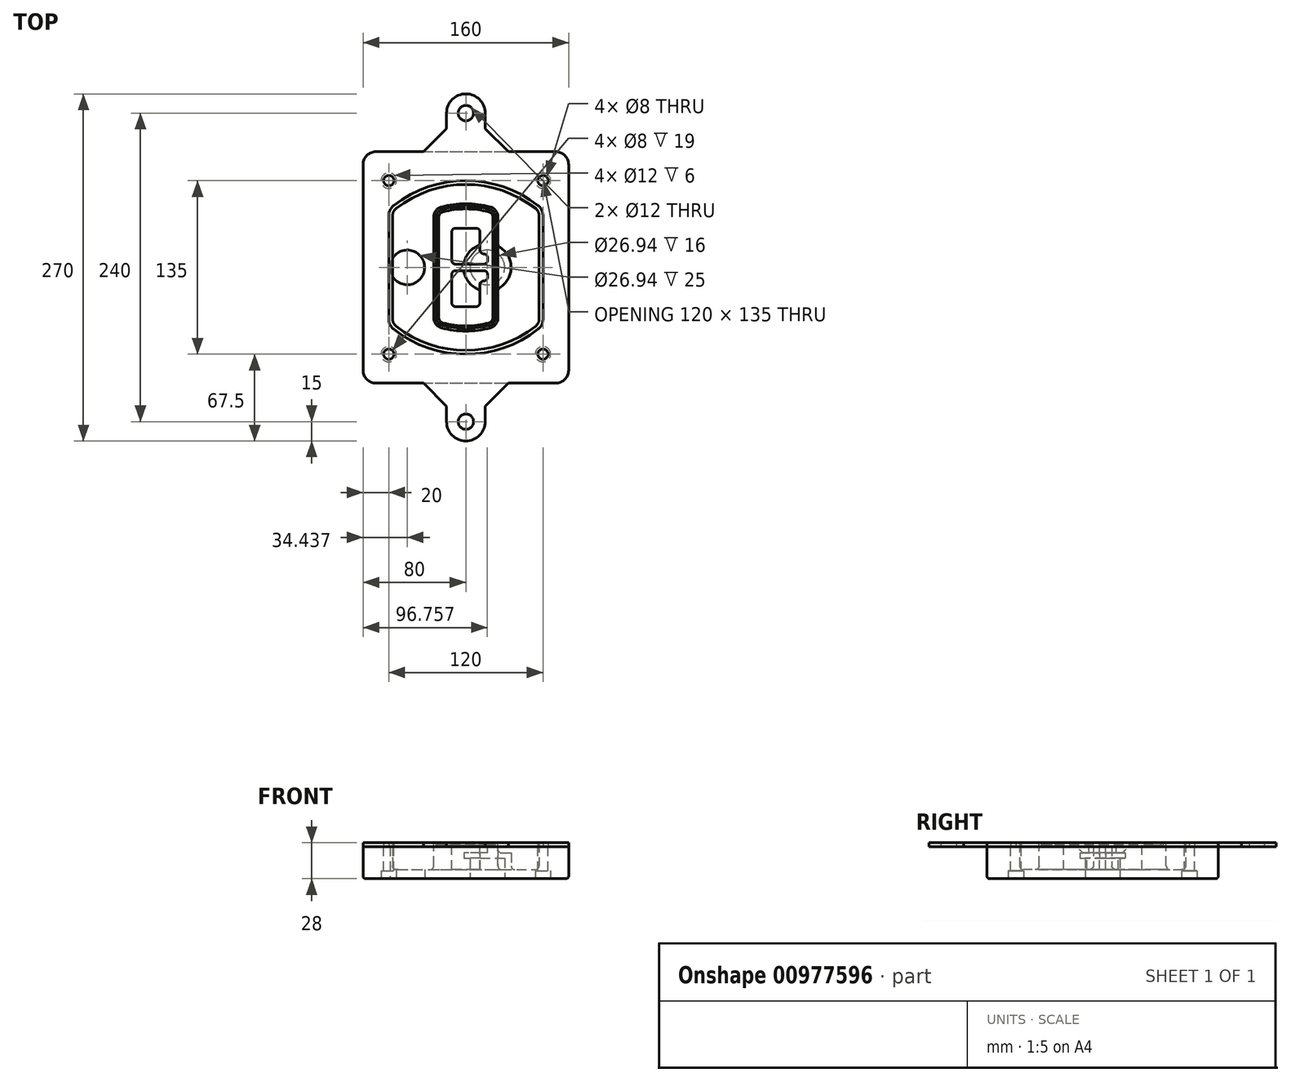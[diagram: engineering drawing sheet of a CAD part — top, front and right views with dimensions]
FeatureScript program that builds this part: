
annotation { "Feature Type Name" : "Feature", "Feature Type Description" : "" }
export const myFeature = defineFeature(function(context is Context, id is Id, definition is map)
    precondition{}
    {
        {
            var Q0;
            Q0=qCreatedBy(makeId("Top.planeOp"),FACE);
            var sketch = newSketch(context, id + "F0", { "sketchPlane" : qUnion([Q0])});
            skPoint(sketch, "E0.rect.middle", {"position": v(0, 0) * mm});
            skLineSegment(sketch, "E1.bottom", {"start": v(-70, -90) * mm, "end": v(70, -90) * mm});
            skLineSegment(sketch, "E1.top", {"start": v(-70, 90) * mm, "end": v(70, 90) * mm});
            skLineSegment(sketch, "E1.left", {"start": v(-80, -80) * mm, "end": v(-80, 80) * mm});
            skLineSegment(sketch, "E1.right", {"start": v(80, -80) * mm, "end": v(80, 80) * mm});
            skLineSegment(sketch, "E2", {"start": v(-80, 90) * mm, "end": v(80, -90) * mm, "construction": true});
            skLineSegment(sketch, "E3", {"start": v(80, 90) * mm, "end": v(-80, -90) * mm, "construction": true});
            skCircle(sketch, "E4", {"center": v(-60, 67.5) * mm, "radius": 4 * mm});
            skCircle(sketch, "E5", {"center": v(60, 67.5) * mm, "radius": 4 * mm});
            skCircle(sketch, "E6", {"center": v(60, -67.5) * mm, "radius": 4 * mm});
            skCircle(sketch, "E7", {"center": v(-60, -67.5) * mm, "radius": 4 * mm});
            skLineSegment(sketch, "E8", {"start": v(-60, 67.5) * mm, "end": v(60, 67.5) * mm, "construction": true});
            skLineSegment(sketch, "E9", {"start": v(60, 67.5) * mm, "end": v(60, -67.5) * mm, "construction": true});
            skLineSegment(sketch, "E10", {"start": v(60, -67.5) * mm, "end": v(-60, -67.5) * mm, "construction": true});
            skLineSegment(sketch, "E11", {"start": v(-60, -67.5) * mm, "end": v(-60, 67.5) * mm, "construction": true});
            skLineSegment(sketch, "E12", {"start": v(-60, 40.3) * mm, "end": v(-60, -40.3) * mm});
            skLineSegment(sketch, "E13", {"start": v(60, 40.3) * mm, "end": v(60, -40.3) * mm});
            skArc(sketch, "E14", {"start": v(56.15, 48.18) * mm, "mid": v(0, 67.5) * mm, "end": v(-56.15, 48.18) * mm});
            skArc(sketch, "E15", {"start": v(-56.15, -48.18) * mm, "mid": v(0, -67.5) * mm, "end": v(56.15, -48.18) * mm});
            skLineSegment(sketch, "E16", {"start": v(-60, 0) * mm, "end": v(60, 0) * mm, "construction": true});
            skPoint(sketch, "E17.visualSharp", {"position": v(-60, -45) * mm});
            skArc(sketch, "E17.filletArc", {"start": v(-60, -40.3) * mm, "mid": v(-58.99, -44.68) * mm, "end": v(-56.15, -48.18) * mm});
            skPoint(sketch, "E18.visualSharp", {"position": v(-60, 45) * mm});
            skArc(sketch, "E18.filletArc", {"start": v(-56.15, 48.18) * mm, "mid": v(-58.99, 44.68) * mm, "end": v(-60, 40.3) * mm});
            skPoint(sketch, "E19.visualSharp", {"position": v(60, 45) * mm});
            skArc(sketch, "E19.filletArc", {"start": v(60, 40.3) * mm, "mid": v(58.99, 44.68) * mm, "end": v(56.15, 48.18) * mm});
            skPoint(sketch, "E20.visualSharp", {"position": v(60, -45) * mm});
            skArc(sketch, "E20.filletArc", {"start": v(56.15, -48.18) * mm, "mid": v(58.99, -44.68) * mm, "end": v(60, -40.3) * mm});
            skPoint(sketch, "E21.visualSharp", {"position": v(-80, 90) * mm});
            skArc(sketch, "E21.filletArc", {"start": v(-70, 90) * mm, "mid": v(-77.07, 87.07) * mm, "end": v(-80, 80) * mm});
            skPoint(sketch, "E22.visualSharp", {"position": v(80, 90) * mm});
            skArc(sketch, "E22.filletArc", {"start": v(80, 80) * mm, "mid": v(77.07, 87.07) * mm, "end": v(70, 90) * mm});
            skPoint(sketch, "E23.visualSharp", {"position": v(80, -90) * mm});
            skArc(sketch, "E23.filletArc", {"start": v(70, -90) * mm, "mid": v(77.07, -87.07) * mm, "end": v(80, -80) * mm});
            skPoint(sketch, "E24.visualSharp", {"position": v(-80, -90) * mm});
            skArc(sketch, "E24.filletArc", {"start": v(-80, -80) * mm, "mid": v(-77.07, -87.07) * mm, "end": v(-70, -90) * mm});
            skArc(sketch, "E25.0", {"start": v(57, 40.3) * mm, "mid": v(56.3, 43.36) * mm, "end": v(54.3, 45.81) * mm});
            skLineSegment(sketch, "E25.1", {"start": v(57, 40.3) * mm, "end": v(57, -40.3) * mm});
            skArc(sketch, "E25.2", {"start": v(54.3, -45.81) * mm, "mid": v(56.3, -43.36) * mm, "end": v(57, -40.3) * mm});
            skArc(sketch, "E25.3", {"start": v(-54.3, -45.81) * mm, "mid": v(0, -64.5) * mm, "end": v(54.3, -45.81) * mm});
            skArc(sketch, "E25.4", {"start": v(-57, -40.3) * mm, "mid": v(-56.3, -43.36) * mm, "end": v(-54.3, -45.81) * mm});
            skArc(sketch, "E25.5", {"start": v(54.3, 45.81) * mm, "mid": v(0, 64.5) * mm, "end": v(-54.3, 45.81) * mm});
            skLineSegment(sketch, "E25.6", {"start": v(-57, 40.3) * mm, "end": v(-57, -40.3) * mm});
            skArc(sketch, "E25.7", {"start": v(-54.3, 45.81) * mm, "mid": v(-56.3, 43.36) * mm, "end": v(-57, 40.3) * mm});
            skArc(sketch, "E26.0", {"start": v(-58.62, 51.33) * mm, "mid": v(-62.58, 46.43) * mm, "end": v(-64, 40.3) * mm});
            skArc(sketch, "E26.1", {"start": v(58.62, 51.33) * mm, "mid": v(0, 71.5) * mm, "end": v(-58.62, 51.33) * mm});
            skArc(sketch, "E26.2", {"start": v(64, 40.3) * mm, "mid": v(62.58, 46.43) * mm, "end": v(58.62, 51.33) * mm});
            skLineSegment(sketch, "E26.3", {"start": v(64, 40.3) * mm, "end": v(64, -40.3) * mm});
            skArc(sketch, "E26.4", {"start": v(58.62, -51.33) * mm, "mid": v(62.58, -46.43) * mm, "end": v(64, -40.3) * mm});
            skLineSegment(sketch, "E26.5", {"start": v(-64, 40.3) * mm, "end": v(-64, -40.3) * mm});
            skArc(sketch, "E26.6", {"start": v(-58.62, -51.33) * mm, "mid": v(0, -71.5) * mm, "end": v(58.62, -51.33) * mm});
            skArc(sketch, "E26.7", {"start": v(-64, -40.3) * mm, "mid": v(-62.58, -46.43) * mm, "end": v(-58.62, -51.33) * mm});
            skSolve(sketch);
        }
        {
            var Q0;
            Q0=makeQuery(id+"F0.imprint","IMPRINT",FACE,{"disambiguationData":[TD([[makeQuery(id+"F0.imprint","IMPRINT",EDGE,{"derivedFrom":sQuery(id+"F0.wireOp",EDGE,"E1.bottom")}),1.0]])]});
            var Q1;
            Q1=makeQuery(id+"F0.imprint","IMPRINT",FACE,{"disambiguationData":[TD([[makeQuery(id+"F0.imprint","IMPRINT",EDGE,{"derivedFrom":sQuery(id+"F0.wireOp",EDGE,"E12")}),1.0]])]});
            var Q2;
            Q2=makeQuery(id+"F0.imprint","IMPRINT",FACE,{"disambiguationData":[TD([[makeQuery(id+"F0.imprint","IMPRINT",EDGE,{"derivedFrom":sQuery(id+"F0.wireOp",EDGE,"E25.0")}),1.0]])]});
            var Q3;
            Q3=makeQuery(id+"F0.imprint","IMPRINT",FACE,{"disambiguationData":[TD([[makeQuery(id+"F0.imprint","IMPRINT",EDGE,{"derivedFrom":sQuery(id+"F0.wireOp",EDGE,"E12")}),-1.0]])]});
            extrude(context, id + "F1", {"entities" : qUnion([Q0, Q1, Q2, Q3]), "oppositeDirection" : true, "depth" : 25 * mm});
        }
        {
            var Q0;
            Q0=makeQuery(id+"F0.imprint","IMPRINT",FACE,{"disambiguationData":[TD([[makeQuery(id+"F0.imprint","IMPRINT",EDGE,{"derivedFrom":sQuery(id+"F0.wireOp",EDGE,"E12")}),1.0]])]});
            extrude(context, id + "F2", {"entities" : qUnion([Q0]), "operationType" : NewBodyOperationType.ADD, "depth" : 3 * mm});
        }
        {
            var Q0;
            Q0=makeQuery(id+"F0.imprint","IMPRINT",FACE,{"disambiguationData":[TD([[makeQuery(id+"F0.imprint","IMPRINT",EDGE,{"derivedFrom":sQuery(id+"F0.wireOp",EDGE,"E25.0")}),1.0]])]});
            extrude(context, id + "F3", {"entities" : qUnion([Q0]), "operationType" : NewBodyOperationType.REMOVE, "oppositeDirection" : true, "depth" : 18 * mm});
        }
        {
            var Q0;
            Q0=makeQuery(id+"F2.opExtrude","CAP_FACE",FACE,{"disambiguationData":[OSD([sQuery(id+"F0.wireOp",EDGE,"E12"),sQuery(id+"F0.wireOp",EDGE,"E13"),sQuery(id+"F0.wireOp",EDGE,"E14"),sQuery(id+"F0.wireOp",EDGE,"E15"),sQuery(id+"F0.wireOp",EDGE,"E17.filletArc"),sQuery(id+"F0.wireOp",EDGE,"E18.filletArc"),sQuery(id+"F0.wireOp",EDGE,"E19.filletArc"),sQuery(id+"F0.wireOp",EDGE,"E20.filletArc"),sQuery(id+"F0.wireOp",EDGE,"E25.0"),sQuery(id+"F0.wireOp",EDGE,"E25.1"),sQuery(id+"F0.wireOp",EDGE,"E25.2"),sQuery(id+"F0.wireOp",EDGE,"E25.3"),sQuery(id+"F0.wireOp",EDGE,"E25.4"),sQuery(id+"F0.wireOp",EDGE,"E25.5"),sQuery(id+"F0.wireOp",EDGE,"E25.6"),sQuery(id+"F0.wireOp",EDGE,"E25.7")])],"isStart":false});
            var sketch = newSketch(context, id + "F4", { "sketchPlane" : qUnion([Q0])});
            skArc(sketch, "E27.0", {"start": v(-19.08, -46.97) * mm, "mid": v(0, -49.5) * mm, "end": v(19.08, -46.97) * mm});
            skArc(sketch, "E28.0", {"start": v(19.08, 46.97) * mm, "mid": v(0, 49.5) * mm, "end": v(-19.08, 46.97) * mm});
            skLineSegment(sketch, "E29", {"start": v(-25, 39.25) * mm, "end": v(-25, -39.25) * mm});
            skLineSegment(sketch, "E30", {"start": v(25, 39.25) * mm, "end": v(25, -39.25) * mm});
            skLineSegment(sketch, "E31", {"start": v(-25, 45.1) * mm, "end": v(25, 45.1) * mm, "construction": true});
            skLineSegment(sketch, "E32", {"start": v(-25, -45.1) * mm, "end": v(25, -45.1) * mm, "construction": true});
            skPoint(sketch, "E33.visualSharp", {"position": v(-25, 45.1) * mm});
            skArc(sketch, "E33.filletArc", {"start": v(-19.08, 46.97) * mm, "mid": v(-23.35, 44.11) * mm, "end": v(-25, 39.25) * mm});
            skPoint(sketch, "E34.visualSharp", {"position": v(25, 45.1) * mm});
            skArc(sketch, "E34.filletArc", {"start": v(25, 39.25) * mm, "mid": v(23.35, 44.11) * mm, "end": v(19.08, 46.97) * mm});
            skPoint(sketch, "E35.visualSharp", {"position": v(25, -45.1) * mm});
            skArc(sketch, "E35.filletArc", {"start": v(19.08, -46.97) * mm, "mid": v(23.35, -44.11) * mm, "end": v(25, -39.25) * mm});
            skPoint(sketch, "E36.visualSharp", {"position": v(-25, -45.1) * mm});
            skArc(sketch, "E36.filletArc", {"start": v(-25, -39.25) * mm, "mid": v(-23.35, -44.11) * mm, "end": v(-19.08, -46.97) * mm});
            skArc(sketch, "E37.0", {"start": v(54.3, 45.81) * mm, "mid": v(0, 64.5) * mm, "end": v(-54.3, 45.81) * mm});
            skArc(sketch, "E37.1", {"start": v(-54.3, 45.81) * mm, "mid": v(-56.3, 43.36) * mm, "end": v(-57, 40.3) * mm});
            skLineSegment(sketch, "E37.2", {"start": v(-57, 40.3) * mm, "end": v(-57, -40.3) * mm});
            skArc(sketch, "E37.3", {"start": v(-57, -40.3) * mm, "mid": v(-56.3, -43.36) * mm, "end": v(-54.3, -45.81) * mm});
            skArc(sketch, "E37.4", {"start": v(-54.3, -45.81) * mm, "mid": v(0, -64.5) * mm, "end": v(54.3, -45.81) * mm});
            skArc(sketch, "E37.5", {"start": v(54.3, -45.81) * mm, "mid": v(56.3, -43.36) * mm, "end": v(57, -40.3) * mm});
            skLineSegment(sketch, "E37.6", {"start": v(57, 40.3) * mm, "end": v(57, -40.3) * mm});
            skArc(sketch, "E37.7", {"start": v(57, 40.3) * mm, "mid": v(56.3, 43.36) * mm, "end": v(54.3, 45.81) * mm});
            skLineSegment(sketch, "E38.0", {"start": v(23, 39.25) * mm, "end": v(23, -39.25) * mm});
            skArc(sketch, "E38.1", {"start": v(18.56, -45.04) * mm, "mid": v(21.76, -42.9) * mm, "end": v(23, -39.25) * mm});
            skArc(sketch, "E38.2", {"start": v(-18.56, -45.04) * mm, "mid": v(0, -47.5) * mm, "end": v(18.56, -45.04) * mm});
            skArc(sketch, "E38.3", {"start": v(-23, -39.25) * mm, "mid": v(-21.76, -42.9) * mm, "end": v(-18.56, -45.04) * mm});
            skLineSegment(sketch, "E38.4", {"start": v(-23, 39.25) * mm, "end": v(-23, -39.25) * mm});
            skArc(sketch, "E38.5", {"start": v(23, 39.25) * mm, "mid": v(21.76, 42.9) * mm, "end": v(18.56, 45.04) * mm});
            skArc(sketch, "E38.6", {"start": v(-18.56, 45.04) * mm, "mid": v(-21.76, 42.9) * mm, "end": v(-23, 39.25) * mm});
            skArc(sketch, "E38.7", {"start": v(18.56, 45.04) * mm, "mid": v(0, 47.5) * mm, "end": v(-18.56, 45.04) * mm});
            skArc(sketch, "E39.0", {"start": v(21, 39.25) * mm, "mid": v(20.18, 41.68) * mm, "end": v(18.04, 43.1) * mm});
            skLineSegment(sketch, "E39.1", {"start": v(21, 39.25) * mm, "end": v(21, -39.25) * mm});
            skArc(sketch, "E39.2", {"start": v(18.04, -43.1) * mm, "mid": v(20.18, -41.68) * mm, "end": v(21, -39.25) * mm});
            skArc(sketch, "E39.3", {"start": v(-18.04, -43.1) * mm, "mid": v(0, -45.5) * mm, "end": v(18.04, -43.1) * mm});
            skArc(sketch, "E39.4", {"start": v(-21, -39.25) * mm, "mid": v(-20.18, -41.68) * mm, "end": v(-18.04, -43.1) * mm});
            skArc(sketch, "E39.5", {"start": v(18.04, 43.1) * mm, "mid": v(0, 45.5) * mm, "end": v(-18.04, 43.1) * mm});
            skLineSegment(sketch, "E39.6", {"start": v(-21, 39.25) * mm, "end": v(-21, -39.25) * mm});
            skArc(sketch, "E39.7", {"start": v(-18.04, 43.1) * mm, "mid": v(-20.18, 41.68) * mm, "end": v(-21, 39.25) * mm});
            skLineSegment(sketch, "E40", {"start": v(-25, 0) * mm, "end": v(25, 0) * mm, "construction": true});
            skLineSegment(sketch, "E41", {"start": v(-11, 5.5) * mm, "end": v(-11, 27.5) * mm});
            skLineSegment(sketch, "E42", {"start": v(-8, 30.5) * mm, "end": v(8, 30.5) * mm});
            skLineSegment(sketch, "E43", {"start": v(11, 27.5) * mm, "end": v(11, 13.5) * mm});
            skLineSegment(sketch, "E44", {"start": v(14, 10.5) * mm, "end": v(14, 10.5) * mm});
            skLineSegment(sketch, "E45", {"start": v(17, 7.5) * mm, "end": v(17, 5.5) * mm});
            skLineSegment(sketch, "E46", {"start": v(14, 2.5) * mm, "end": v(-8, 2.5) * mm});
            skPoint(sketch, "E47.visualSharp", {"position": v(-11, 30.5) * mm});
            skArc(sketch, "E47.filletArc", {"start": v(-8, 30.5) * mm, "mid": v(-10.12, 29.62) * mm, "end": v(-11, 27.5) * mm});
            skPoint(sketch, "E48.visualSharp", {"position": v(11, 30.5) * mm});
            skArc(sketch, "E48.filletArc", {"start": v(11, 27.5) * mm, "mid": v(10.12, 29.62) * mm, "end": v(8, 30.5) * mm});
            skPoint(sketch, "E49.visualSharp", {"position": v(11, 10.5) * mm});
            skArc(sketch, "E49.filletArc", {"start": v(11, 13.5) * mm, "mid": v(11.88, 11.38) * mm, "end": v(14, 10.5) * mm});
            skPoint(sketch, "E50.visualSharp", {"position": v(17, 10.5) * mm});
            skArc(sketch, "E50.filletArc", {"start": v(17, 7.5) * mm, "mid": v(16.12, 9.62) * mm, "end": v(14, 10.5) * mm});
            skPoint(sketch, "E51.visualSharp", {"position": v(17, 2.5) * mm});
            skArc(sketch, "E51.filletArc", {"start": v(14, 2.5) * mm, "mid": v(16.12, 3.38) * mm, "end": v(17, 5.5) * mm});
            skPoint(sketch, "E52.visualSharp", {"position": v(-11, 2.5) * mm});
            skArc(sketch, "E52.filletArc", {"start": v(-11, 5.5) * mm, "mid": v(-10.12, 3.38) * mm, "end": v(-8, 2.5) * mm});
            skLineSegment(sketch, "E53.0.MirrorCS", {"start": v(14, -2.5) * mm, "end": v(-8, -2.5) * mm});
            skArc(sketch, "E54.0.MirrorCS", {"start": v(-11, -5.5) * mm, "mid": v(-10.12, -3.38) * mm, "end": v(-8, -2.5) * mm});
            skLineSegment(sketch, "E55.0.MirrorCS", {"start": v(-11, -5.5) * mm, "end": v(-11, -27.5) * mm});
            skArc(sketch, "E56.0.MirrorCS", {"start": v(-8, -30.5) * mm, "mid": v(-10.12, -29.62) * mm, "end": v(-11, -27.5) * mm});
            skLineSegment(sketch, "E57.0.MirrorCS", {"start": v(-8, -30.5) * mm, "end": v(8, -30.5) * mm});
            skArc(sketch, "E58.0.MirrorCS", {"start": v(11, -27.5) * mm, "mid": v(10.12, -29.62) * mm, "end": v(8, -30.5) * mm});
            skLineSegment(sketch, "E59.0.MirrorCS", {"start": v(11, -27.5) * mm, "end": v(11, -13.5) * mm});
            skArc(sketch, "E60.0.MirrorCS", {"start": v(11, -13.5) * mm, "mid": v(11.88, -11.38) * mm, "end": v(14, -10.5) * mm});
            skArc(sketch, "E61.0.MirrorCS", {"start": v(17, -7.5) * mm, "mid": v(16.12, -9.62) * mm, "end": v(14, -10.5) * mm});
            skLineSegment(sketch, "E62.0.MirrorCS", {"start": v(17, -7.5) * mm, "end": v(17, -5.5) * mm});
            skArc(sketch, "E63.0.MirrorCS", {"start": v(14, -2.5) * mm, "mid": v(16.12, -3.38) * mm, "end": v(17, -5.5) * mm});
            skSolve(sketch);
        }
        {
            var Q0;
            Q0=makeQuery(id+"F4.imprint","IMPRINT",FACE,{"disambiguationData":[TD([[makeQuery(id+"F4.imprint","IMPRINT",EDGE,{"derivedFrom":sQuery(id+"F4.wireOp",EDGE,"E27.0")}),1.0]])]});
            var Q1;
            Q1=makeQuery(id+"F4.imprint","IMPRINT",FACE,{"disambiguationData":[TD([[makeQuery(id+"F4.imprint","IMPRINT",EDGE,{"derivedFrom":sQuery(id+"F4.wireOp",EDGE,"E38.0")}),-1.0]])]});
            var Q2;
            Q2=makeQuery(id+"F4.imprint","IMPRINT",FACE,{"disambiguationData":[TD([[makeQuery(id+"F4.imprint","IMPRINT",EDGE,{"derivedFrom":sQuery(id+"F4.wireOp",EDGE,"E39.0")}),1.0]])]});
            extrude(context, id + "F5", {"entities" : qUnion([Q0, Q1, Q2]), "operationType" : NewBodyOperationType.ADD, "endBound" : BoundingType.UP_TO_NEXT, "oppositeDirection" : true, "depth" : 25 * mm});
        }
        {
            var Q0;
            Q0=makeQuery(id+"F4.imprint","IMPRINT",FACE,{"disambiguationData":[TD([[makeQuery(id+"F4.imprint","IMPRINT",EDGE,{"derivedFrom":sQuery(id+"F4.wireOp",EDGE,"E38.0")}),-1.0]])]});
            extrude(context, id + "F6", {"entities" : qUnion([Q0]), "operationType" : NewBodyOperationType.REMOVE, "oppositeDirection" : true, "depth" : 2 * mm});
        }
        {
            var Q0;
            Q0=makeQuery(id+"F1.opExtrude","CAP_FACE",FACE,{"disambiguationData":[OSD([sQuery(id+"F0.wireOp",EDGE,"E1.bottom"),sQuery(id+"F0.wireOp",EDGE,"E1.top"),sQuery(id+"F0.wireOp",EDGE,"E1.left"),sQuery(id+"F0.wireOp",EDGE,"E1.right"),sQuery(id+"F0.wireOp",EDGE,"E4"),sQuery(id+"F0.wireOp",EDGE,"E5"),sQuery(id+"F0.wireOp",EDGE,"E6"),sQuery(id+"F0.wireOp",EDGE,"E7"),sQuery(id+"F0.wireOp",EDGE,"E21.filletArc"),sQuery(id+"F0.wireOp",EDGE,"E22.filletArc"),sQuery(id+"F0.wireOp",EDGE,"E23.filletArc"),sQuery(id+"F0.wireOp",EDGE,"E24.filletArc")])],"isStart":false});
            var sketch = newSketch(context, id + "F7", { "sketchPlane" : qUnion([Q0])});
            skCircle(sketch, "E64", {"center": v(16.76, 0) * mm, "radius": 13.47 * mm});
            skCircle(sketch, "E65", {"center": v(-45.56, 0) * mm, "radius": 13.47 * mm});
            skLineSegment(sketch, "E66", {"start": v(80, 0) * mm, "end": v(-80, 0) * mm});
            skCircle(sketch, "E67", {"center": v(16.76, 0) * mm, "radius": 18.47 * mm});
            skCircle(sketch, "E68", {"center": v(60, -67.5) * mm, "radius": 6 * mm});
            skCircle(sketch, "E69", {"center": v(-60, -67.5) * mm, "radius": 6 * mm});
            skCircle(sketch, "E70", {"center": v(-60, 67.5) * mm, "radius": 6 * mm});
            skCircle(sketch, "E71", {"center": v(60, 67.5) * mm, "radius": 6 * mm});
            skSolve(sketch);
        }
        {
            var Q0;
            {var subQ1=sQuery(id+"F7.wireOp",EDGE,"E66");var subQ4=sQuery(id+"F7.wireOp",EDGE,"E64");var subQ6=makeQuery(id+"F7.imprint","INTERSECT",VERTEX,{"disambiguationData":[OD(0.0)],"derivedFrom":[subQ4,subQ1]});Q0=makeQuery(id+"F7.imprint","IMPRINT",FACE,{"disambiguationData":[TD([[makeQuery(id+"F7.imprint","IMPRINT",EDGE,{"disambiguationData":[TD([[subQ6,-1.0]])],"derivedFrom":subQ4}),-1.0]])]});}
            var Q1;
            {var subQ0=sQuery(id+"F7.wireOp",EDGE,"E66");var subQ1=sQuery(id+"F7.wireOp",EDGE,"E64");var subQ3=makeQuery(id+"F7.imprint","INTERSECT",VERTEX,{"disambiguationData":[OD(0.0)],"derivedFrom":[subQ1,subQ0]});Q1=makeQuery(id+"F7.imprint","IMPRINT",FACE,{"disambiguationData":[TD([[makeQuery(id+"F7.imprint","IMPRINT",EDGE,{"disambiguationData":[TD([[subQ3,-1.0]])],"derivedFrom":subQ1}),1.0]])]});}
            var Q2;
            {var subQ0=sQuery(id+"F7.wireOp",EDGE,"E66");var subQ1=sQuery(id+"F7.wireOp",EDGE,"E64");var subQ3=makeQuery(id+"F7.imprint","INTERSECT",VERTEX,{"disambiguationData":[OD(0.0)],"derivedFrom":[subQ1,subQ0]});Q2=makeQuery(id+"F7.imprint","IMPRINT",FACE,{"disambiguationData":[TD([[makeQuery(id+"F7.imprint","IMPRINT",EDGE,{"disambiguationData":[TD([[subQ3,1.0]])],"derivedFrom":subQ1}),1.0]])]});}
            var Q3;
            {var subQ1=sQuery(id+"F7.wireOp",EDGE,"E66");var subQ4=sQuery(id+"F7.wireOp",EDGE,"E64");var subQ6=makeQuery(id+"F7.imprint","INTERSECT",VERTEX,{"disambiguationData":[OD(0.0)],"derivedFrom":[subQ4,subQ1]});Q3=makeQuery(id+"F7.imprint","IMPRINT",FACE,{"disambiguationData":[TD([[makeQuery(id+"F7.imprint","IMPRINT",EDGE,{"disambiguationData":[TD([[subQ6,1.0]])],"derivedFrom":subQ4}),-1.0]])]});}
            extrude(context, id + "F8", {"entities" : qUnion([Q0, Q1, Q2, Q3]), "operationType" : NewBodyOperationType.ADD, "oppositeDirection" : true, "depth" : 20 * mm});
        }
        {
            var Q0;
            {var subQ0=sQuery(id+"F7.wireOp",EDGE,"E66");var subQ1=sQuery(id+"F7.wireOp",EDGE,"E64");var subQ3=makeQuery(id+"F7.imprint","INTERSECT",VERTEX,{"disambiguationData":[OD(0.0)],"derivedFrom":[subQ1,subQ0]});Q0=makeQuery(id+"F7.imprint","IMPRINT",FACE,{"disambiguationData":[TD([[makeQuery(id+"F7.imprint","IMPRINT",EDGE,{"disambiguationData":[TD([[subQ3,-1.0]])],"derivedFrom":subQ1}),1.0]])]});}
            var Q1;
            {var subQ0=sQuery(id+"F7.wireOp",EDGE,"E66");var subQ1=sQuery(id+"F7.wireOp",EDGE,"E64");var subQ3=makeQuery(id+"F7.imprint","INTERSECT",VERTEX,{"disambiguationData":[OD(0.0)],"derivedFrom":[subQ1,subQ0]});Q1=makeQuery(id+"F7.imprint","IMPRINT",FACE,{"disambiguationData":[TD([[makeQuery(id+"F7.imprint","IMPRINT",EDGE,{"disambiguationData":[TD([[subQ3,1.0]])],"derivedFrom":subQ1}),1.0]])]});}
            extrude(context, id + "F9", {"entities" : qUnion([Q0, Q1]), "operationType" : NewBodyOperationType.REMOVE, "oppositeDirection" : true, "depth" : 16 * mm});
        }
        {
            var Q0;
            {var subQ0=sQuery(id+"F7.wireOp",EDGE,"E66");var subQ1=sQuery(id+"F7.wireOp",EDGE,"E65");var subQ3=makeQuery(id+"F7.imprint","INTERSECT",VERTEX,{"disambiguationData":[OD(0.0)],"derivedFrom":[subQ1,subQ0]});Q0=makeQuery(id+"F7.imprint","IMPRINT",FACE,{"disambiguationData":[TD([[makeQuery(id+"F7.imprint","IMPRINT",EDGE,{"disambiguationData":[TD([[subQ3,-1.0]])],"derivedFrom":subQ1}),1.0]])]});}
            var Q1;
            {var subQ0=sQuery(id+"F7.wireOp",EDGE,"E66");var subQ1=sQuery(id+"F7.wireOp",EDGE,"E65");var subQ3=makeQuery(id+"F7.imprint","INTERSECT",VERTEX,{"disambiguationData":[OD(0.0)],"derivedFrom":[subQ1,subQ0]});Q1=makeQuery(id+"F7.imprint","IMPRINT",FACE,{"disambiguationData":[TD([[makeQuery(id+"F7.imprint","IMPRINT",EDGE,{"disambiguationData":[TD([[subQ3,1.0]])],"derivedFrom":subQ1}),1.0]])]});}
            extrude(context, id + "F10", {"entities" : qUnion([Q0, Q1]), "operationType" : NewBodyOperationType.REMOVE, "oppositeDirection" : true, "depth" : 25 * mm});
        }
        {
            var Q0;
            Q0=makeQuery(id+"F7.imprint","IMPRINT",FACE,{"disambiguationData":[TD([[makeQuery(id+"F7.imprint","IMPRINT",EDGE,{"derivedFrom":sQuery(id+"F7.wireOp",EDGE,"E68")}),1.0]])]});
            var Q1;
            Q1=makeQuery(id+"F7.imprint","IMPRINT",FACE,{"disambiguationData":[TD([[makeQuery(id+"F7.imprint","IMPRINT",EDGE,{"derivedFrom":makeQuery(id+"F1.opExtrude","CAP_EDGE",EDGE,{"disambiguationData":[OSD([sQuery(id+"F0.wireOp",EDGE,"E5")])],"isStart":false})}),-1.0]])]});
            var Q2;
            Q2=makeQuery(id+"F7.imprint","IMPRINT",FACE,{"disambiguationData":[TD([[makeQuery(id+"F7.imprint","IMPRINT",EDGE,{"derivedFrom":sQuery(id+"F7.wireOp",EDGE,"E69")}),1.0]])]});
            var Q3;
            Q3=makeQuery(id+"F7.imprint","IMPRINT",FACE,{"disambiguationData":[TD([[makeQuery(id+"F7.imprint","IMPRINT",EDGE,{"derivedFrom":makeQuery(id+"F1.opExtrude","CAP_EDGE",EDGE,{"disambiguationData":[OSD([sQuery(id+"F0.wireOp",EDGE,"E4")])],"isStart":false})}),-1.0]])]});
            var Q4;
            Q4=makeQuery(id+"F7.imprint","IMPRINT",FACE,{"disambiguationData":[TD([[makeQuery(id+"F7.imprint","IMPRINT",EDGE,{"derivedFrom":sQuery(id+"F7.wireOp",EDGE,"E70")}),1.0]])]});
            var Q5;
            Q5=makeQuery(id+"F7.imprint","IMPRINT",FACE,{"disambiguationData":[TD([[makeQuery(id+"F7.imprint","IMPRINT",EDGE,{"derivedFrom":makeQuery(id+"F1.opExtrude","CAP_EDGE",EDGE,{"disambiguationData":[OSD([sQuery(id+"F0.wireOp",EDGE,"E7")])],"isStart":false})}),-1.0]])]});
            var Q6;
            Q6=makeQuery(id+"F7.imprint","IMPRINT",FACE,{"disambiguationData":[TD([[makeQuery(id+"F7.imprint","IMPRINT",EDGE,{"derivedFrom":sQuery(id+"F7.wireOp",EDGE,"E71")}),1.0]])]});
            var Q7;
            Q7=makeQuery(id+"F7.imprint","IMPRINT",FACE,{"disambiguationData":[TD([[makeQuery(id+"F7.imprint","IMPRINT",EDGE,{"derivedFrom":makeQuery(id+"F1.opExtrude","CAP_EDGE",EDGE,{"disambiguationData":[OSD([sQuery(id+"F0.wireOp",EDGE,"E6")])],"isStart":false})}),-1.0]])]});
            extrude(context, id + "F11", {"entities" : qUnion([Q0, Q1, Q2, Q3, Q4, Q5, Q6, Q7]), "operationType" : NewBodyOperationType.REMOVE, "oppositeDirection" : true, "depth" : 6 * mm});
        }
        {
            var Q0;
            Q0=makeQuery(id+"F9.boolean.opBoolean","COPY",FACE,{"derivedFrom":makeQuery(id+"F9.opExtrude","CAP_FACE",FACE,{"disambiguationData":[OSD([sQuery(id+"F7.wireOp",EDGE,"E64")])],"isStart":false})});
            var sketch = newSketch(context, id + "F12", { "sketchPlane" : qUnion([Q0])});
            skArc(sketch, "E72.0", {"start": v(11, 17.55) * mm, "mid": v(2.57, 11.82) * mm, "end": v(-1.54, 2.5) * mm});
            skArc(sketch, "E72.1", {"start": v(-1.54, -2.5) * mm, "mid": v(2.57, -11.82) * mm, "end": v(11, -17.55) * mm});
            skLineSegment(sketch, "E73", {"start": v(-1.54, -2.5) * mm, "end": v(14, -2.5) * mm});
            skLineSegment(sketch, "E74.0", {"start": v(14, 2.5) * mm, "end": v(-1.54, 2.5) * mm});
            skArc(sketch, "E74.1", {"start": v(14, 2.5) * mm, "mid": v(16.12, 3.38) * mm, "end": v(17, 5.5) * mm});
            skLineSegment(sketch, "E74.2", {"start": v(17, 7.5) * mm, "end": v(17, 5.5) * mm});
            skArc(sketch, "E74.3", {"start": v(17, 7.5) * mm, "mid": v(16.12, 9.62) * mm, "end": v(14, 10.5) * mm});
            skArc(sketch, "E74.4", {"start": v(11, 13.5) * mm, "mid": v(11.88, 11.38) * mm, "end": v(14, 10.5) * mm});
            skLineSegment(sketch, "E74.5", {"start": v(11, 17.55) * mm, "end": v(11, 13.5) * mm});
            skLineSegment(sketch, "E74.7", {"start": v(14, -2.5) * mm, "end": v(-1.54, -2.5) * mm});
            skArc(sketch, "E74.8", {"start": v(14, -2.5) * mm, "mid": v(16.12, -3.38) * mm, "end": v(17, -5.5) * mm});
            skLineSegment(sketch, "E74.9", {"start": v(17, -7.5) * mm, "end": v(17, -5.5) * mm});
            skArc(sketch, "E74.10", {"start": v(17, -7.5) * mm, "mid": v(16.12, -9.62) * mm, "end": v(14, -10.5) * mm});
            skArc(sketch, "E74.11", {"start": v(11, -13.5) * mm, "mid": v(11.88, -11.38) * mm, "end": v(14, -10.5) * mm});
            skLineSegment(sketch, "E74.12", {"start": v(11, -17.55) * mm, "end": v(11, -13.5) * mm});
            skPoint(sketch, "E75.orphan", {"position": v(11, -27.5) * mm});
            skPoint(sketch, "E76.orphan", {"position": v(-8, -2.5) * mm});
            skPoint(sketch, "E77.orphan", {"position": v(-8, 2.5) * mm});
            skPoint(sketch, "E78.orphan", {"position": v(11, 27.5) * mm});
            skSolve(sketch);
        }
        {
            var Q0;
            {var subQ7=sQuery(id+"F12.wireOp",EDGE,"E72.0");var subQ14=sQuery(id+"F12.wireOp",EDGE,"E72.1");var subQ16=sQuery(id+"F12.wireOp",EDGE,"E74.1");var subQ18=sQuery(id+"F12.wireOp",EDGE,"E74.8");Q0=qUnion([makeQuery(id+"F12.imprint","IMPRINT",FACE,{"disambiguationData":[TD([[makeQuery(id+"F12.imprint","IMPRINT",EDGE,{"derivedFrom":subQ7}),1.0]])]}),makeQuery(id+"F12.imprint","IMPRINT",FACE,{"disambiguationData":[TD([[makeQuery(id+"F12.imprint","IMPRINT",EDGE,{"derivedFrom":subQ14}),1.0]])]}),makeQuery(id+"F12.imprint","IMPRINT",FACE,{"disambiguationData":[TD([[makeQuery(id+"F12.imprint","IMPRINT",EDGE,{"derivedFrom":subQ16}),1.0]])]}),makeQuery(id+"F12.imprint","IMPRINT",FACE,{"disambiguationData":[TD([[makeQuery(id+"F12.imprint","IMPRINT",EDGE,{"derivedFrom":subQ18}),-1.0]])]})]);}
            var Q1;
            Q1=makeQuery(id+"F5.boolean.opBoolean","SPLIT",FACE,{"disambiguationData":[TD([makeQuery(id+"F5.opExtrude","SWEPT_FACE",FACE,{"disambiguationData":[OSD([sQuery(id+"F4.wireOp",EDGE,"E41")])]})])],"derivedFrom":makeQuery(id+"F3.boolean.opBoolean","COPY",FACE,{"derivedFrom":makeQuery(id+"F3.opExtrude","CAP_FACE",FACE,{"disambiguationData":[OSD([sQuery(id+"F0.wireOp",EDGE,"E25.0"),sQuery(id+"F0.wireOp",EDGE,"E25.1"),sQuery(id+"F0.wireOp",EDGE,"E25.2"),sQuery(id+"F0.wireOp",EDGE,"E25.3"),sQuery(id+"F0.wireOp",EDGE,"E25.4"),sQuery(id+"F0.wireOp",EDGE,"E25.5"),sQuery(id+"F0.wireOp",EDGE,"E25.6"),sQuery(id+"F0.wireOp",EDGE,"E25.7")])],"isStart":false})})});
            extrude(context, id + "F13", {"entities" : qUnion([Q0]), "operationType" : NewBodyOperationType.REMOVE, "endBound" : BoundingType.UP_TO_SURFACE, "endBoundEntityFace" : qUnion([Q1]), "depth" : 25 * mm});
        }
        {
            var Q0;
            Q0=makeQuery(id+"F3.boolean.opBoolean","COPY",EDGE,{"derivedFrom":makeQuery(id+"F3.opExtrude","CAP_EDGE",EDGE,{"disambiguationData":[OSD([sQuery(id+"F0.wireOp",EDGE,"E25.6")])],"isStart":false})});
            var Q1;
            Q1=makeQuery(id+"F8.boolean.opBoolean","INTERSECT",EDGE,{"derivedFrom":[makeQuery(id+"F5.opExtrude","SWEPT_FACE",FACE,{"disambiguationData":[OSD([sQuery(id+"F4.wireOp",EDGE,"E30")])]}),makeQuery(id+"F8.opExtrude","CAP_FACE",FACE,{"disambiguationData":[OSD([sQuery(id+"F7.wireOp",EDGE,"E67")])],"isStart":false})]});
            var Q2;
            Q2=makeQuery(id+"F8.boolean.opBoolean","INTERSECT",EDGE,{"disambiguationData":[OD(1.0)],"derivedFrom":[makeQuery(id+"F5.opExtrude","SWEPT_FACE",FACE,{"disambiguationData":[OSD([sQuery(id+"F4.wireOp",EDGE,"E30")])]}),makeQuery(id+"F8.opExtrude","SWEPT_FACE",FACE,{"disambiguationData":[OSD([sQuery(id+"F7.wireOp",EDGE,"E67")])]})]});
            var Q3;
            {var subQ0=sQuery(id+"F4.wireOp",EDGE,"E30");Q3=makeQuery(id+"F8.boolean.opBoolean","SPLIT",EDGE,{"disambiguationData":[TD([makeQuery(id+"F5.opExtrude","SWEPT_FACE",FACE,{"disambiguationData":[OSD([sQuery(id+"F4.wireOp",EDGE,"E35.filletArc")])]})])],"derivedFrom":makeQuery(id+"F5.opExtrude","CAP_EDGE",EDGE,{"disambiguationData":[OSD([subQ0])],"isStart":false})});}
            var Q4;
            {var subQ0=sQuery(id+"F0.wireOp",EDGE,"E25.7");var subQ1=sQuery(id+"F0.wireOp",EDGE,"E25.1");var subQ2=sQuery(id+"F0.wireOp",EDGE,"E25.6");var subQ3=sQuery(id+"F0.wireOp",EDGE,"E25.5");var subQ4=sQuery(id+"F0.wireOp",EDGE,"E25.4");var subQ5=sQuery(id+"F0.wireOp",EDGE,"E25.0");var subQ6=sQuery(id+"F0.wireOp",EDGE,"E25.2");var subQ7=sQuery(id+"F0.wireOp",EDGE,"E25.3");Q4=makeQuery(id+"F8.boolean.opBoolean","INTERSECT",EDGE,{"derivedFrom":[makeQuery(id+"F5.boolean.opBoolean","SPLIT",FACE,{"disambiguationData":[TD([makeQuery(id+"F2.opExtrude","SWEPT_FACE",FACE,{"disambiguationData":[OSD([subQ5])]})])],"derivedFrom":makeQuery(id+"F3.boolean.opBoolean","COPY",FACE,{"derivedFrom":makeQuery(id+"F3.opExtrude","CAP_FACE",FACE,{"disambiguationData":[OSD([subQ5,subQ1,subQ6,subQ7,subQ4,subQ3,subQ2,subQ0])],"isStart":false})})}),makeQuery(id+"F8.opExtrude","SWEPT_FACE",FACE,{"disambiguationData":[OSD([sQuery(id+"F7.wireOp",EDGE,"E67")])]})]});}
            var Q5;
            Q5=makeQuery(id+"F8.boolean.opBoolean","INTERSECT",EDGE,{"disambiguationData":[OD(0.0)],"derivedFrom":[makeQuery(id+"F5.opExtrude","SWEPT_FACE",FACE,{"disambiguationData":[OSD([sQuery(id+"F4.wireOp",EDGE,"E30")])]}),makeQuery(id+"F8.opExtrude","SWEPT_FACE",FACE,{"disambiguationData":[OSD([sQuery(id+"F7.wireOp",EDGE,"E67")])]})]});
            fillet(context, id + "F14", {"entities" : qUnion([Q0, Q1, Q2, Q3, Q4, Q5]), "radius" : 3 * mm, "tangentPropagation" : true, "allowEdgeOverflow" : false});
        }
        {
            var Q0;
            Q0=makeQuery(id+"F1.opExtrude","CAP_EDGE",EDGE,{"disambiguationData":[OSD([sQuery(id+"F0.wireOp",EDGE,"E1.bottom")])],"isStart":false});
            fillet(context, id + "F15", {"entities" : qUnion([Q0]), "radius" : 2 * mm, "tangentPropagation" : true, "allowEdgeOverflow" : false});
        }
        {
            var Q0;
            {var subQ0=sQuery(id+"F0.wireOp",EDGE,"E21.filletArc");var subQ1=sQuery(id+"F0.wireOp",EDGE,"E7");var subQ2=sQuery(id+"F0.wireOp",EDGE,"E6");var subQ3=sQuery(id+"F0.wireOp",EDGE,"E5");var subQ4=sQuery(id+"F0.wireOp",EDGE,"E4");var subQ5=sQuery(id+"F0.wireOp",EDGE,"E22.filletArc");var subQ6=sQuery(id+"F0.wireOp",EDGE,"E1.bottom");var subQ7=sQuery(id+"F0.wireOp",EDGE,"E1.right");var subQ8=sQuery(id+"F0.wireOp",EDGE,"E1.top");var subQ9=sQuery(id+"F0.wireOp",EDGE,"E1.left");var subQ10=sQuery(id+"F0.wireOp",EDGE,"E23.filletArc");var subQ11=sQuery(id+"F0.wireOp",EDGE,"E24.filletArc");Q0=makeQuery(id+"F2.boolean.opBoolean","SPLIT",FACE,{"disambiguationData":[TD([makeQuery(id+"F1.opExtrude","SWEPT_FACE",FACE,{"disambiguationData":[OSD([subQ6])]})])],"derivedFrom":makeQuery(id+"F1.opExtrude","CAP_FACE",FACE,{"disambiguationData":[OSD([subQ6,subQ8,subQ9,subQ7,subQ4,subQ3,subQ2,subQ1,subQ0,subQ5,subQ10,subQ11])],"isStart":true})});}
            var sketch = newSketch(context, id + "F16", { "sketchPlane" : qUnion([Q0])});
            skLineSegment(sketch, "E79.0", {"start": v(-70, 90) * mm, "end": v(70, 90) * mm});
            skArc(sketch, "E79.1", {"start": v(-70, 90) * mm, "mid": v(-77.07, 87.07) * mm, "end": v(-80, 80) * mm});
            skLineSegment(sketch, "E79.2", {"start": v(-80, -80) * mm, "end": v(-80, 80) * mm});
            skArc(sketch, "E79.3", {"start": v(-80, -80) * mm, "mid": v(-77.07, -87.07) * mm, "end": v(-70, -90) * mm});
            skLineSegment(sketch, "E79.4", {"start": v(-70, -90) * mm, "end": v(70, -90) * mm});
            skLineSegment(sketch, "E79.5", {"start": v(-60, 40.3) * mm, "end": v(-60, -40.3) * mm});
            skArc(sketch, "E79.6", {"start": v(-56.15, 48.18) * mm, "mid": v(-58.99, 44.68) * mm, "end": v(-60, 40.3) * mm});
            skArc(sketch, "E79.7", {"start": v(-60, -40.3) * mm, "mid": v(-58.99, -44.68) * mm, "end": v(-56.15, -48.18) * mm});
            skArc(sketch, "E79.8", {"start": v(-56.15, -48.18) * mm, "mid": v(0, -67.5) * mm, "end": v(56.15, -48.18) * mm});
            skArc(sketch, "E79.9", {"start": v(70, -90) * mm, "mid": v(77.07, -87.07) * mm, "end": v(80, -80) * mm});
            skLineSegment(sketch, "E79.10", {"start": v(80, -80) * mm, "end": v(80, 80) * mm});
            skArc(sketch, "E79.11", {"start": v(56.15, -48.18) * mm, "mid": v(58.99, -44.68) * mm, "end": v(60, -40.3) * mm});
            skLineSegment(sketch, "E79.12", {"start": v(60, 40.3) * mm, "end": v(60, -40.3) * mm});
            skArc(sketch, "E79.13", {"start": v(56.15, 48.18) * mm, "mid": v(0, 67.5) * mm, "end": v(-56.15, 48.18) * mm});
            skArc(sketch, "E79.14", {"start": v(60, 40.3) * mm, "mid": v(58.99, 44.68) * mm, "end": v(56.15, 48.18) * mm});
            skArc(sketch, "E79.15", {"start": v(80, 80) * mm, "mid": v(77.07, 87.07) * mm, "end": v(70, 90) * mm});
            skLineSegment(sketch, "E80", {"start": v(0, 90) * mm, "end": v(0, 120) * mm, "construction": true});
            skCircle(sketch, "E81", {"center": v(0, 120) * mm, "radius": 6 * mm});
            skArc(sketch, "E82", {"start": v(15, 120) * mm, "mid": v(0, 135) * mm, "end": v(-15, 120) * mm});
            skLineSegment(sketch, "E83", {"start": v(-15, 120) * mm, "end": v(-15, 108) * mm});
            skLineSegment(sketch, "E84", {"start": v(15, 120) * mm, "end": v(15, 108) * mm});
            skLineSegment(sketch, "E85", {"start": v(15, 108) * mm, "end": v(33, 90) * mm});
            skLineSegment(sketch, "E86.MirrorCS", {"start": v(-15, 108) * mm, "end": v(-33, 90) * mm});
            skLineSegment(sketch, "E87", {"start": v(-80, 0) * mm, "end": v(80, 0) * mm, "construction": true});
            skLineSegment(sketch, "E88.MirrorCS", {"start": v(-15, -120) * mm, "end": v(-15, -108) * mm});
            skLineSegment(sketch, "E89.MirrorCS", {"start": v(15, -120) * mm, "end": v(15, -108) * mm});
            skCircle(sketch, "E90.MirrorC", {"center": v(0, -120) * mm, "radius": 6 * mm});
            skLineSegment(sketch, "E91.MirrorCS", {"start": v(0, -90) * mm, "end": v(0, -120) * mm, "construction": true});
            skLineSegment(sketch, "E92.MirrorCS", {"start": v(15, -108) * mm, "end": v(33, -90) * mm});
            skLineSegment(sketch, "E93.MirrorCS", {"start": v(-15, -108) * mm, "end": v(-33, -90) * mm});
            skArc(sketch, "E94.MirrorCS", {"start": v(15, -120) * mm, "mid": v(0, -135) * mm, "end": v(-15, -120) * mm});
            skSolve(sketch);
        }
        {
            var Q0;
            Q0=makeQuery(id+"F16.imprint","IMPRINT",FACE,{"disambiguationData":[TD([[makeQuery(id+"F16.imprint","IMPRINT",EDGE,{"derivedFrom":sQuery(id+"F16.wireOp",EDGE,"E88.MirrorCS")}),-1.0]])]});
            var Q1;
            Q1=makeQuery(id+"F16.imprint","IMPRINT",FACE,{"disambiguationData":[TD([[makeQuery(id+"F16.imprint","IMPRINT",EDGE,{"derivedFrom":sQuery(id+"F16.wireOp",EDGE,"E81")}),-1.0]])]});
            var Q2;
            {var subQ2=sQuery(id+"F16.wireOp",EDGE,"E79.1");Q2=makeQuery(id+"F16.imprint","IMPRINT",FACE,{"disambiguationData":[TD([[makeQuery(id+"F16.imprint","IMPRINT",EDGE,{"derivedFrom":subQ2}),1.0]])]});}
            var Q3;
            Q3=makeQuery(id+"F2.opExtrude","CAP_FACE",FACE,{"disambiguationData":[OSD([sQuery(id+"F0.wireOp",EDGE,"E12"),sQuery(id+"F0.wireOp",EDGE,"E13"),sQuery(id+"F0.wireOp",EDGE,"E14"),sQuery(id+"F0.wireOp",EDGE,"E15"),sQuery(id+"F0.wireOp",EDGE,"E17.filletArc"),sQuery(id+"F0.wireOp",EDGE,"E18.filletArc"),sQuery(id+"F0.wireOp",EDGE,"E19.filletArc"),sQuery(id+"F0.wireOp",EDGE,"E20.filletArc"),sQuery(id+"F0.wireOp",EDGE,"E25.0"),sQuery(id+"F0.wireOp",EDGE,"E25.1"),sQuery(id+"F0.wireOp",EDGE,"E25.2"),sQuery(id+"F0.wireOp",EDGE,"E25.3"),sQuery(id+"F0.wireOp",EDGE,"E25.4"),sQuery(id+"F0.wireOp",EDGE,"E25.5"),sQuery(id+"F0.wireOp",EDGE,"E25.6"),sQuery(id+"F0.wireOp",EDGE,"E25.7")])],"isStart":false});
            extrude(context, id + "F17", {"entities" : qUnion([Q0, Q1, Q2]), "endBound" : BoundingType.UP_TO_SURFACE, "depth" : 25 * mm, "endBoundEntityFace" : qUnion([Q3]), "offsetDistance" : 25 * mm});
        }
    });
